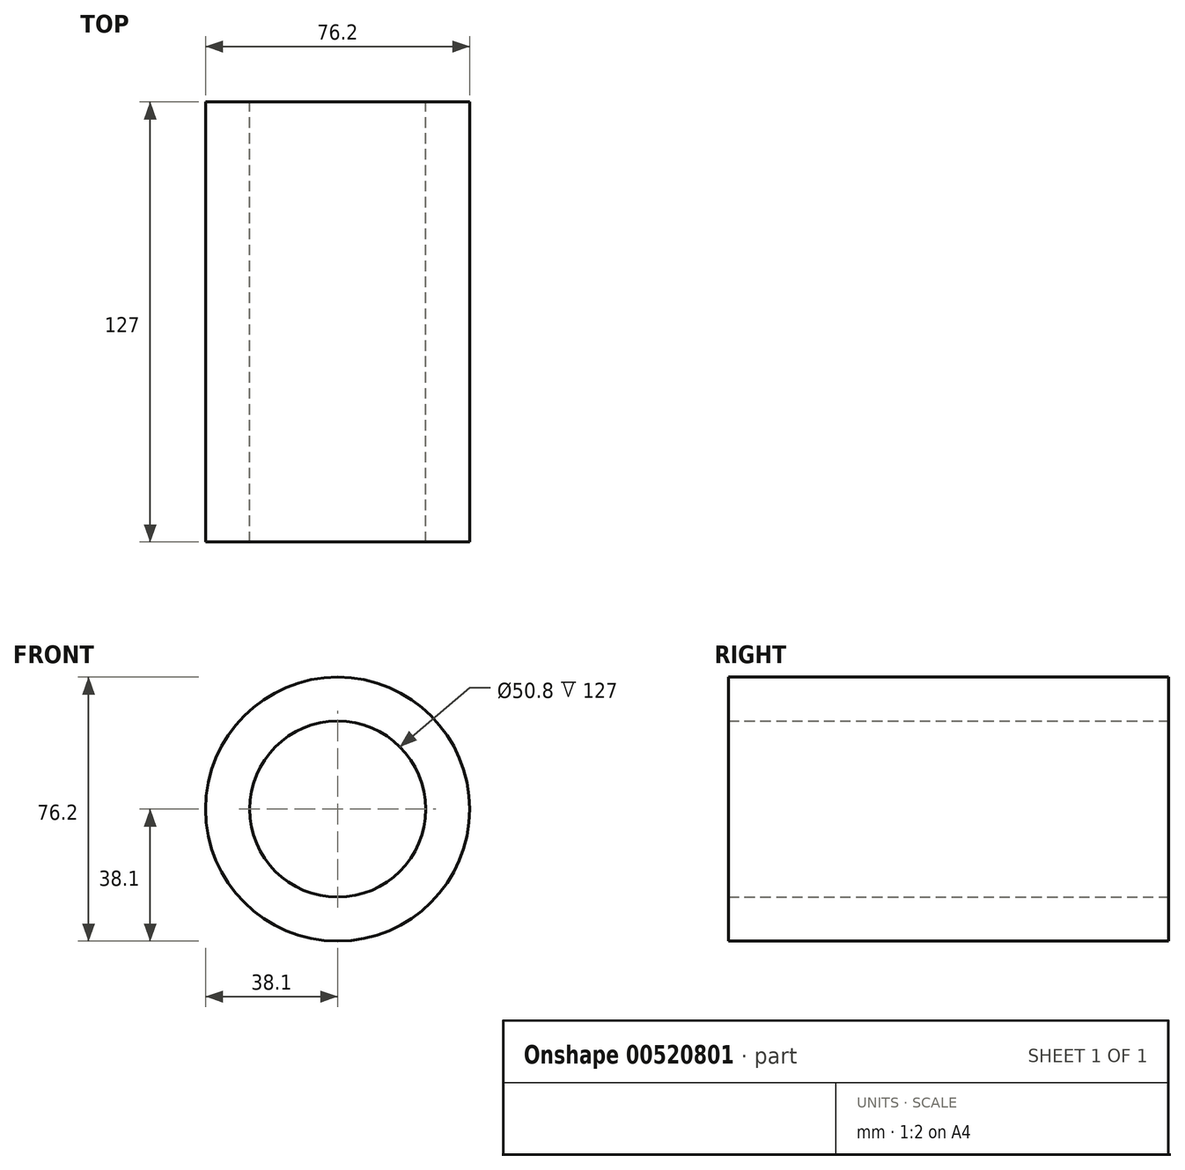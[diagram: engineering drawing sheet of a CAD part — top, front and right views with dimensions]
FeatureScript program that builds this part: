
annotation { "Feature Type Name" : "Feature", "Feature Type Description" : "" }
export const myFeature = defineFeature(function(context is Context, id is Id, definition is map)
    precondition{}
    {
        {
            var Q0;
            Q0=qCreatedBy(makeId("Front.planeOp"),FACE);
            var sketch = newSketch(context, id + "F0", { "sketchPlane" : qUnion([Q0])});
            skCircle(sketch, "E0", {"center": v(0, 0) * mm, "radius": 38.1 * mm});
            skCircle(sketch, "E1", {"center": v(0, 0) * mm, "radius": 25.4 * mm});
            skSolve(sketch);
        }
        {
            var Q0;
            Q0 = qSketchRegion(id + "F0", true);
            extrude(context, id + "F1", {"entities" : qUnion([Q0]), "depth" : 127 * mm, "offsetDistance" : 25.4 * mm});
        }
    });
